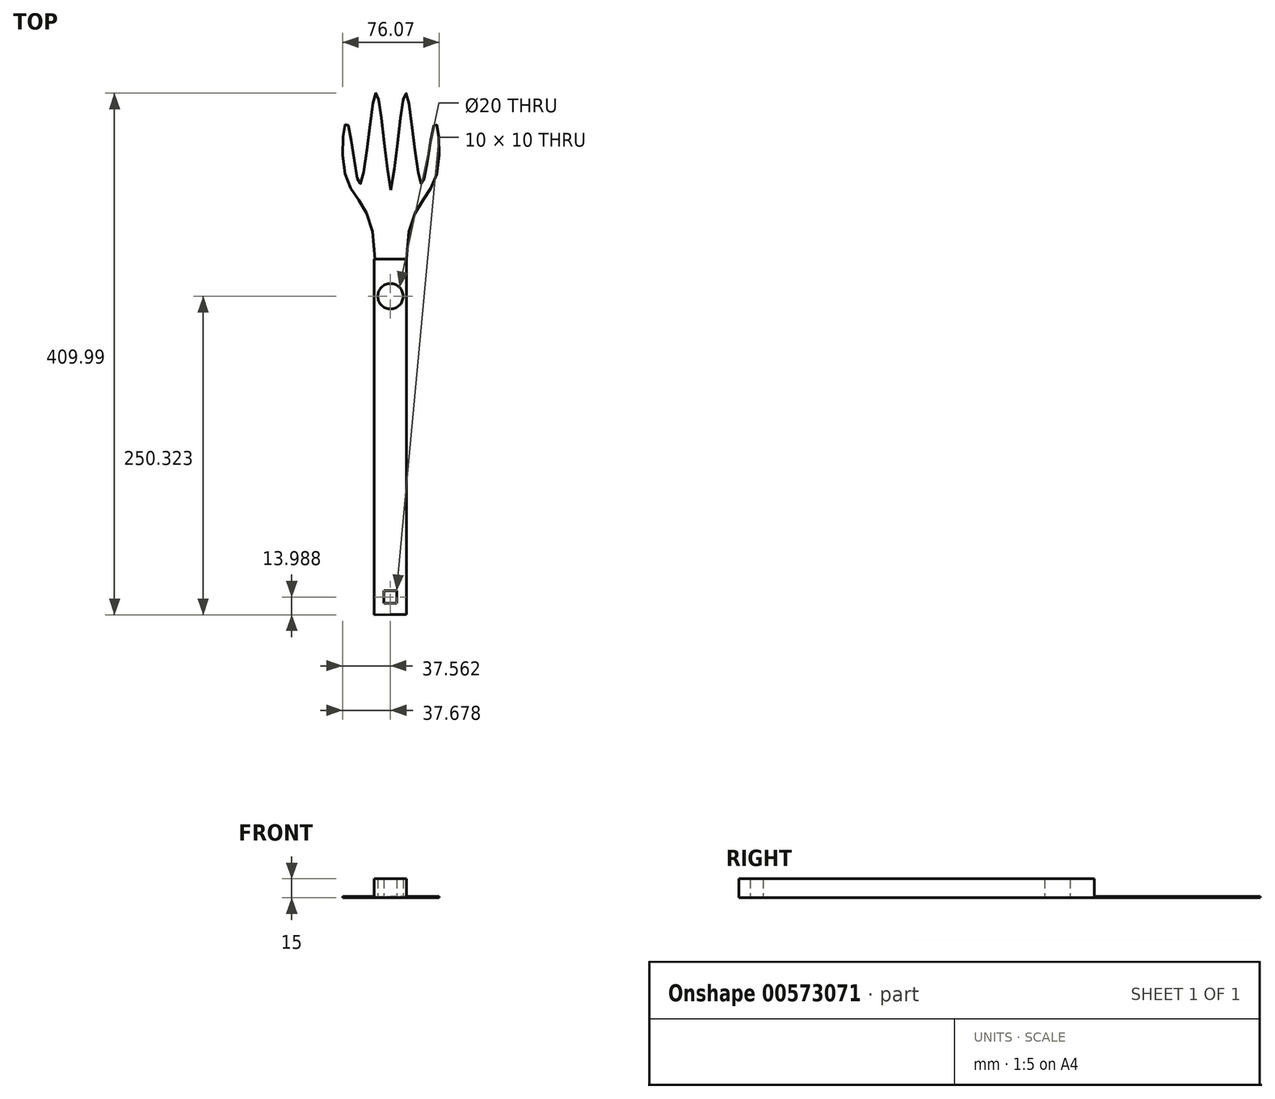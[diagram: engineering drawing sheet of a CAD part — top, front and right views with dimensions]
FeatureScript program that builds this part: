
annotation { "Feature Type Name" : "Feature", "Feature Type Description" : "" }
export const myFeature = defineFeature(function(context is Context, id is Id, definition is map)
    precondition{}
    {
        {
            var Q0;
            Q0=qCreatedBy(makeId("Top.planeOp"),FACE);
            var sketch = newSketch(context, id + "F0", { "sketchPlane" : qUnion([Q0])});
            skLineSegment(sketch, "E0.bottom", {"start": v(-25.32, 102.88) * mm, "end": v(0.08, 102.84) * mm});
            skLineSegment(sketch, "E0.left", {"start": v(-25.32, 102.88) * mm, "end": v(-25.4, -176.7) * mm});
            skLineSegment(sketch, "E0.right", {"start": v(0.08, 102.84) * mm, "end": v(0, -176.64) * mm});
            skCircle(sketch, "E1", {"center": v(-12.57, 73.62) * mm, "radius": 10 * mm});
            skLineSegment(sketch, "E2", {"start": v(-25.4, -176.7) * mm, "end": v(-12.7, -176.66) * mm});
            skLineSegment(sketch, "E3", {"start": v(0, -176.64) * mm, "end": v(-12.7, -176.66) * mm});
            skLineSegment(sketch, "E4", {"start": v(-12.7, -176.66) * mm, "end": v(-12.69, -167.71) * mm});
            skLineSegment(sketch, "E5", {"start": v(-12.69, -167.71) * mm, "end": v(-7.69, -167.71) * mm});
            skLineSegment(sketch, "E6", {"start": v(-7.69, -167.71) * mm, "end": v(-7.69, -157.71) * mm});
            skLineSegment(sketch, "E7", {"start": v(-7.69, -157.71) * mm, "end": v(-17.69, -157.71) * mm});
            skLineSegment(sketch, "E8", {"start": v(-17.69, -157.71) * mm, "end": v(-17.69, -167.71) * mm});
            skLineSegment(sketch, "E9", {"start": v(-17.69, -167.71) * mm, "end": v(-12.69, -167.71) * mm});
            skPoint(sketch, "E10.5.internal.snap0", {"position": v(-12.62, 102.86) * mm});
            skFitSpline(sketch, "E10", {"points": [v(0.08, 102.84) * mm, v(23.65, 169.31) * mm, v(22.14, 209.28) * mm, v(11.97, 161.89) * mm, v(0, 232.95) * mm, v(-12.62, 155.56) * mm], "startDerivative": vector(-1.08, 605.55) * mm, "endDerivative": vector(-70.82, -286.92) * mm});
            skFitSpline(sketch, "E11.MirrorCS", {"points": [v(-24.74, 102.87) * mm, v(-48.14, 169.4) * mm, v(-46.53, 209.37) * mm, v(-36.48, 161.95) * mm, v(-24.32, 232.98) * mm, v(-11.9, 155.56) * mm], "startDerivative": vector(2.67, 605.55) * mm, "endDerivative": vector(70.06, -287.1) * mm});
            skSolve(sketch);
        }
        {
            var Q0;
            {var subQ0=sQuery(id+"F0.wireOp",EDGE,"E0.left");Q0=makeQuery(id+"F0.imprint","IMPRINT",FACE,{"disambiguationData":[TD([[makeQuery(id+"F0.imprint","IMPRINT",EDGE,{"derivedFrom":subQ0}),1.0]])]});}
            extrude(context, id + "F1", {"entities" : qUnion([Q0]), "depth" : 15 * mm, "offsetDistance" : 25.4 * mm});
        }
        {
            var Q0;
            {var subQ0=sQuery(id+"F0.wireOp",EDGE,"E10");var subQ3=sQuery(id+"F0.wireOp",EDGE,"E11.MirrorCS");var subQ5=makeQuery(id+"F0.imprint","INTERSECT",VERTEX,{"derivedFrom":[subQ0,subQ3]});Q0=makeQuery(id+"F0.imprint","IMPRINT",FACE,{"disambiguationData":[TD([[makeQuery(id+"F0.imprint","IMPRINT",EDGE,{"disambiguationData":[TD([[subQ5,1.0]])],"derivedFrom":subQ3}),-1.0]])]});}
            extrude(context, id + "F2", {"entities" : qUnion([Q0]), "operationType" : NewBodyOperationType.ADD, "depth" : 1 * mm, "offsetDistance" : 25.4 * mm});
        }
        {
            var Q0;
            Q0=sQuery(id+"F0.wireOp",EDGE,"E1");
            extrude(context, id + "F3", {"bodyType" : ToolBodyType.SURFACE, "surfaceEntities" : qUnion([Q0]), "depth" : 22 * mm, "offsetDistance" : 25.4 * mm});
        }
    });
